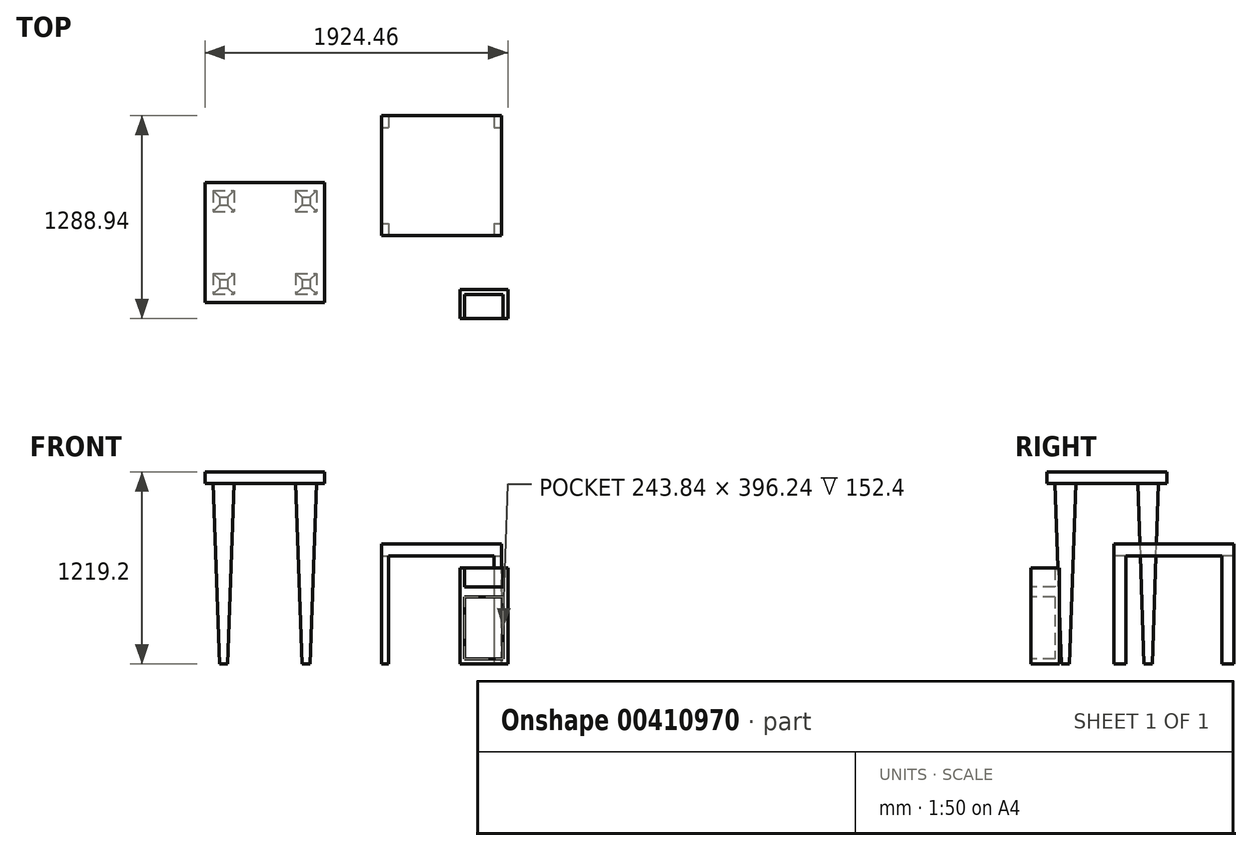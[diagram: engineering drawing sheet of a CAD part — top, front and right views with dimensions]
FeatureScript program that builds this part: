
annotation { "Feature Type Name" : "Feature", "Feature Type Description" : "" }
export const myFeature = defineFeature(function(context is Context, id is Id, definition is map)
    precondition{}
    {
        {
            var Q0;
            Q0=qCreatedBy(makeId("Top.planeOp"),FACE);
            var sketch = newSketch(context, id + "F0", { "sketchPlane" : qUnion([Q0])});
            skLineSegment(sketch, "E0.bottom", {"start": v(0, 0) * mm, "end": v(762, 0) * mm});
            skLineSegment(sketch, "E0.top", {"start": v(0, 762) * mm, "end": v(762, 762) * mm});
            skLineSegment(sketch, "E0.left", {"start": v(0, 0) * mm, "end": v(0, 762) * mm});
            skLineSegment(sketch, "E0.right", {"start": v(762, 0) * mm, "end": v(762, 762) * mm});
            skSolve(sketch);
        }
        {
            var Q0;
            Q0=makeQuery(id+"F0.imprint","IMPRINT",FACE,{"disambiguationData":[TD([[makeQuery(id+"F0.imprint","IMPRINT",EDGE,{"derivedFrom":sQuery(id+"F0.wireOp",EDGE,"E0.bottom")}),1.0]])]});
            extrude(context, id + "F1", {"entities" : qUnion([Q0]), "depth" : 762 * mm});
        }
        {
            var Q0;
            Q0=makeQuery(id+"F1.opExtrude","SWEPT_FACE",FACE,{"disambiguationData":[OSD([sQuery(id+"F0.wireOp",EDGE,"E0.bottom")])]});
            var sketch = newSketch(context, id + "F2", { "sketchPlane" : qUnion([Q0])});
            skLineSegment(sketch, "E1", {"start": v(45.72, 0) * mm, "end": v(45.72, 685.8) * mm});
            skLineSegment(sketch, "E2", {"start": v(45.72, 685.8) * mm, "end": v(716.28, 685.8) * mm});
            skLineSegment(sketch, "E3", {"start": v(716.28, 685.8) * mm, "end": v(716.28, 0) * mm});
            skSolve(sketch);
        }
        {
            var Q0;
            {var subQ0=sQuery(id+"F2.wireOp",EDGE,"E1");Q0=makeQuery(id+"F2.imprint","IMPRINT",FACE,{"disambiguationData":[TD([[makeQuery(id+"F2.imprint","IMPRINT",EDGE,{"derivedFrom":subQ0}),-1.0]])]});}
            extrude(context, id + "F3", {"entities" : qUnion([Q0]), "operationType" : NewBodyOperationType.REMOVE, "endBound" : BoundingType.THROUGH_ALL, "oppositeDirection" : true, "depth" : 30.48 * mm});
        }
        {
            var Q0;
            Q0=makeQuery(id+"F1.opExtrude","SWEPT_FACE",FACE,{"disambiguationData":[OSD([sQuery(id+"F0.wireOp",EDGE,"E0.right")])]});
            var sketch = newSketch(context, id + "F4", { "sketchPlane" : qUnion([Q0])});
            skLineSegment(sketch, "E4", {"start": v(76.2, 0) * mm, "end": v(76.2, 685.8) * mm});
            skLineSegment(sketch, "E5", {"start": v(76.2, 685.8) * mm, "end": v(685.8, 685.8) * mm});
            skLineSegment(sketch, "E6", {"start": v(685.8, 685.8) * mm, "end": v(685.8, 0) * mm});
            skSolve(sketch);
        }
        {
            var Q0;
            {var subQ0=sQuery(id+"F4.wireOp",EDGE,"E4");Q0=makeQuery(id+"F4.imprint","IMPRINT",FACE,{"disambiguationData":[TD([[makeQuery(id+"F4.imprint","IMPRINT",EDGE,{"derivedFrom":subQ0}),-1.0]])]});}
            extrude(context, id + "F5", {"entities" : qUnion([Q0]), "operationType" : NewBodyOperationType.REMOVE, "endBound" : BoundingType.THROUGH_ALL, "oppositeDirection" : true, "depth" : 30.48 * mm});
        }
        {
            var Q0;
            Q0=qCreatedBy(makeId("Top.planeOp"),FACE);
            var sketch = newSketch(context, id + "F6", { "sketchPlane" : qUnion([Q0])});
            skLineSegment(sketch, "E7.bottom", {"start": v(-1121.94, 336.68) * mm, "end": v(-359.94, 336.68) * mm});
            skLineSegment(sketch, "E7.top", {"start": v(-1121.94, -425.32) * mm, "end": v(-359.94, -425.32) * mm});
            skLineSegment(sketch, "E7.left", {"start": v(-1121.94, 336.68) * mm, "end": v(-1121.94, -425.32) * mm});
            skLineSegment(sketch, "E7.right", {"start": v(-359.94, 336.68) * mm, "end": v(-359.94, -425.32) * mm});
            skSolve(sketch);
        }
        {
            var Q0;
            Q0=makeQuery(id+"F6.imprint","IMPRINT",FACE,{"disambiguationData":[TD([[makeQuery(id+"F6.imprint","IMPRINT",EDGE,{"derivedFrom":sQuery(id+"F6.wireOp",EDGE,"E7.bottom")}),-1.0]])]});
            extrude(context, id + "F7", {"entities" : qUnion([Q0]), "depth" : 1219.2 * mm});
        }
        {
            var Q0;
            Q0=makeQuery(id+"F7.opExtrude","SWEPT_FACE",FACE,{"disambiguationData":[OSD([sQuery(id+"F6.wireOp",EDGE,"E7.top")])]});
            var sketch = newSketch(context, id + "F8", { "sketchPlane" : qUnion([Q0])});
            skLineSegment(sketch, "E8", {"start": v(-1121.94, 1147.84) * mm, "end": v(-1069.6, 1147.84) * mm});
            skLineSegment(sketch, "E9", {"start": v(-1069.6, 1147.84) * mm, "end": v(-1028.68, 0) * mm});
            skLineSegment(sketch, "E10", {"start": v(-1028.68, 0) * mm, "end": v(-977.53, 0) * mm});
            skLineSegment(sketch, "E11", {"start": v(-977.53, 0) * mm, "end": v(-936.6, 1147.84) * mm});
            skLineSegment(sketch, "E12", {"start": v(-936.6, 1147.84) * mm, "end": v(-704.7, 1147.84) * mm});
            skLineSegment(sketch, "E13", {"start": v(-740.94, 1219.2) * mm, "end": v(-740.94, 0) * mm, "construction": true});
            skLineSegment(sketch, "E14.MirrorCS", {"start": v(-453.2, 0) * mm, "end": v(-504.35, 0) * mm});
            skLineSegment(sketch, "E15.MirrorCS", {"start": v(-359.94, 1147.84) * mm, "end": v(-412.27, 1147.84) * mm});
            skLineSegment(sketch, "E16.MirrorCS", {"start": v(-412.27, 1147.84) * mm, "end": v(-453.2, 0) * mm});
            skLineSegment(sketch, "E17.MirrorCS", {"start": v(-545.28, 1147.84) * mm, "end": v(-704.7, 1147.84) * mm});
            skLineSegment(sketch, "E18.MirrorCS", {"start": v(-504.35, 0) * mm, "end": v(-545.28, 1147.84) * mm});
            skPoint(sketch, "E19.trimOffspring.end.orphan", {"position": v(-777.18, 1147.84) * mm});
            skSolve(sketch);
        }
        {
            var Q0;
            Q0=makeQuery(id+"F7.opExtrude","SWEPT_FACE",FACE,{"disambiguationData":[OSD([sQuery(id+"F6.wireOp",EDGE,"E7.right")])]});
            var sketch = newSketch(context, id + "F9", { "sketchPlane" : qUnion([Q0])});
            skLineSegment(sketch, "E20", {"start": v(-425.32, 1147.84) * mm, "end": v(-372.99, 1147.84) * mm});
            skLineSegment(sketch, "E21", {"start": v(-372.99, 1147.84) * mm, "end": v(-332.06, 0) * mm});
            skLineSegment(sketch, "E22", {"start": v(-332.06, 0) * mm, "end": v(-280.9, 0) * mm});
            skLineSegment(sketch, "E23", {"start": v(-280.9, 0) * mm, "end": v(-239.98, 1147.84) * mm});
            skLineSegment(sketch, "E24", {"start": v(-239.98, 1147.84) * mm, "end": v(-8.07, 1147.84) * mm});
            skLineSegment(sketch, "E25", {"start": v(-44.32, 1108.43) * mm, "end": v(-44.32, -110.77) * mm, "construction": true});
            skLineSegment(sketch, "E26.MirrorCS", {"start": v(243.43, 0) * mm, "end": v(192.27, 0) * mm});
            skLineSegment(sketch, "E27.MirrorCS", {"start": v(336.68, 1147.84) * mm, "end": v(284.35, 1147.84) * mm});
            skLineSegment(sketch, "E28.MirrorCS", {"start": v(284.35, 1147.84) * mm, "end": v(243.43, 0) * mm});
            skLineSegment(sketch, "E29.MirrorCS", {"start": v(151.35, 1147.84) * mm, "end": v(-8.07, 1147.84) * mm});
            skLineSegment(sketch, "E30.MirrorCS", {"start": v(192.27, 0) * mm, "end": v(151.35, 1147.84) * mm});
            skPoint(sketch, "E31.trimOffspring.end.orphan", {"position": v(-80.56, 1147.84) * mm});
            skSolve(sketch);
        }
        {
            var Q0;
            {var subQ0=sQuery(id+"F8.wireOp",EDGE,"E8");Q0=makeQuery(id+"F8.imprint","IMPRINT",FACE,{"disambiguationData":[TD([[makeQuery(id+"F8.imprint","IMPRINT",EDGE,{"derivedFrom":subQ0}),-1.0]])]});}
            var Q1;
            {var subQ1=sQuery(id+"F8.wireOp",EDGE,"E11");Q1=makeQuery(id+"F8.imprint","IMPRINT",FACE,{"disambiguationData":[TD([[makeQuery(id+"F8.imprint","IMPRINT",EDGE,{"derivedFrom":subQ1}),-1.0]])]});}
            var Q2;
            {var subQ0=sQuery(id+"F8.wireOp",EDGE,"E15.MirrorCS");Q2=makeQuery(id+"F8.imprint","IMPRINT",FACE,{"disambiguationData":[TD([[makeQuery(id+"F8.imprint","IMPRINT",EDGE,{"derivedFrom":subQ0}),1.0]])]});}
            extrude(context, id + "F10", {"entities" : qUnion([Q0, Q1, Q2]), "operationType" : NewBodyOperationType.REMOVE, "endBound" : BoundingType.THROUGH_ALL, "oppositeDirection" : true, "depth" : 30.48 * mm});
        }
        {
            var Q0;
            {var subQ0=sQuery(id+"F9.wireOp",EDGE,"E20");Q0=makeQuery(id+"F9.imprint","IMPRINT",FACE,{"disambiguationData":[TD([[makeQuery(id+"F9.imprint","IMPRINT",EDGE,{"derivedFrom":subQ0}),-1.0]])]});}
            var Q1;
            {var subQ1=sQuery(id+"F9.wireOp",EDGE,"E23");Q1=makeQuery(id+"F9.imprint","IMPRINT",FACE,{"disambiguationData":[TD([[makeQuery(id+"F9.imprint","IMPRINT",EDGE,{"derivedFrom":subQ1}),-1.0]])]});}
            var Q2;
            {var subQ0=sQuery(id+"F9.wireOp",EDGE,"E27.MirrorCS");Q2=makeQuery(id+"F9.imprint","IMPRINT",FACE,{"disambiguationData":[TD([[makeQuery(id+"F9.imprint","IMPRINT",EDGE,{"derivedFrom":subQ0}),1.0]])]});}
            extrude(context, id + "F11", {"entities" : qUnion([Q0, Q1, Q2]), "operationType" : NewBodyOperationType.REMOVE, "endBound" : BoundingType.THROUGH_ALL, "oppositeDirection" : true, "depth" : 30.48 * mm});
        }
        {
            var Q0;
            Q0=qCreatedBy(makeId("Top.planeOp"),FACE);
            var sketch = newSketch(context, id + "F12", { "sketchPlane" : qUnion([Q0])});
            skLineSegment(sketch, "E32.bottom", {"start": v(497.72, -344.06) * mm, "end": v(802.52, -344.06) * mm});
            skLineSegment(sketch, "E32.top", {"start": v(497.72, -526.94) * mm, "end": v(802.52, -526.94) * mm});
            skLineSegment(sketch, "E32.left", {"start": v(497.72, -344.06) * mm, "end": v(497.72, -526.94) * mm});
            skLineSegment(sketch, "E32.right", {"start": v(802.52, -344.06) * mm, "end": v(802.52, -526.94) * mm});
            skSolve(sketch);
        }
        {
            var Q0;
            Q0=makeQuery(id+"F12.imprint","IMPRINT",FACE,{"disambiguationData":[TD([[makeQuery(id+"F12.imprint","IMPRINT",EDGE,{"derivedFrom":sQuery(id+"F12.wireOp",EDGE,"E32.bottom")}),-1.0]])]});
            extrude(context, id + "F13", {"entities" : qUnion([Q0]), "depth" : 457.2 * mm});
        }
        {
            var Q0;
            Q0=makeQuery(id+"F13.opExtrude","SWEPT_FACE",FACE,{"disambiguationData":[OSD([sQuery(id+"F12.wireOp",EDGE,"E32.top")])]});
            shell(context, id + "F14", {"entities" : qUnion([Q0]), "thickness" : 30.48 * mm});
        }
        {
            var Q0;
            Q0=makeQuery(id+"F13.opExtrude","CAP_FACE",FACE,{"disambiguationData":[OSD([sQuery(id+"F12.wireOp",EDGE,"E32.bottom"),sQuery(id+"F12.wireOp",EDGE,"E32.top"),sQuery(id+"F12.wireOp",EDGE,"E32.left"),sQuery(id+"F12.wireOp",EDGE,"E32.right")])],"isStart":false});
            var sketch = newSketch(context, id + "F15", { "sketchPlane" : qUnion([Q0])});
            skLineSegment(sketch, "E33.bottom", {"start": v(497.72, -344.06) * mm, "end": v(802.52, -344.06) * mm});
            skLineSegment(sketch, "E33.top", {"start": v(497.72, -526.94) * mm, "end": v(802.52, -526.94) * mm});
            skLineSegment(sketch, "E33.left", {"start": v(497.72, -344.06) * mm, "end": v(497.72, -526.94) * mm});
            skLineSegment(sketch, "E33.right", {"start": v(802.52, -344.06) * mm, "end": v(802.52, -526.94) * mm});
            skSolve(sketch);
        }
        {
            var Q0;
            Q0=makeQuery(id+"F15.imprint","IMPRINT",FACE,{"disambiguationData":[TD([[makeQuery(id+"F15.imprint","IMPRINT",EDGE,{"derivedFrom":sQuery(id+"F15.wireOp",EDGE,"E33.bottom")}),-1.0]])]});
            extrude(context, id + "F16", {"entities" : qUnion([Q0]), "operationType" : NewBodyOperationType.ADD, "depth" : 152.4 * mm});
        }
        {
            var Q0;
            Q0=makeQuery(id+"F16.boolean.opBoolean","MERGE",FACE,{"derivedFrom":[makeQuery(id+"F13.opExtrude","SWEPT_FACE",FACE,{"disambiguationData":[OSD([sQuery(id+"F12.wireOp",EDGE,"E32.top")])]}),makeQuery(id+"F16.opExtrude","SWEPT_FACE",FACE,{"disambiguationData":[OSD([sQuery(id+"F15.wireOp",EDGE,"E33.top")])]})]});
            var sketch = newSketch(context, id + "F17", { "sketchPlane" : qUnion([Q0])});
            skLineSegment(sketch, "E34", {"start": v(497.72, 609.6) * mm, "end": v(528.2, 609.6) * mm});
            skLineSegment(sketch, "E35", {"start": v(528.2, 609.6) * mm, "end": v(528.2, 487.68) * mm});
            skLineSegment(sketch, "E36", {"start": v(528.2, 487.68) * mm, "end": v(772.04, 487.68) * mm});
            skLineSegment(sketch, "E37", {"start": v(772.04, 487.68) * mm, "end": v(772.04, 609.6) * mm});
            skLineSegment(sketch, "E38", {"start": v(772.04, 609.6) * mm, "end": v(802.52, 609.6) * mm});
            skSolve(sketch);
        }
        {
            var Q0;
            {var subQ0=sQuery(id+"F17.wireOp",EDGE,"E35");Q0=makeQuery(id+"F17.imprint","IMPRINT",FACE,{"disambiguationData":[TD([[makeQuery(id+"F17.imprint","IMPRINT",EDGE,{"derivedFrom":subQ0}),1.0]])]});}
            extrude(context, id + "F18", {"entities" : qUnion([Q0]), "operationType" : NewBodyOperationType.REMOVE, "oppositeDirection" : true, "depth" : 152.4 * mm});
        }
    });
